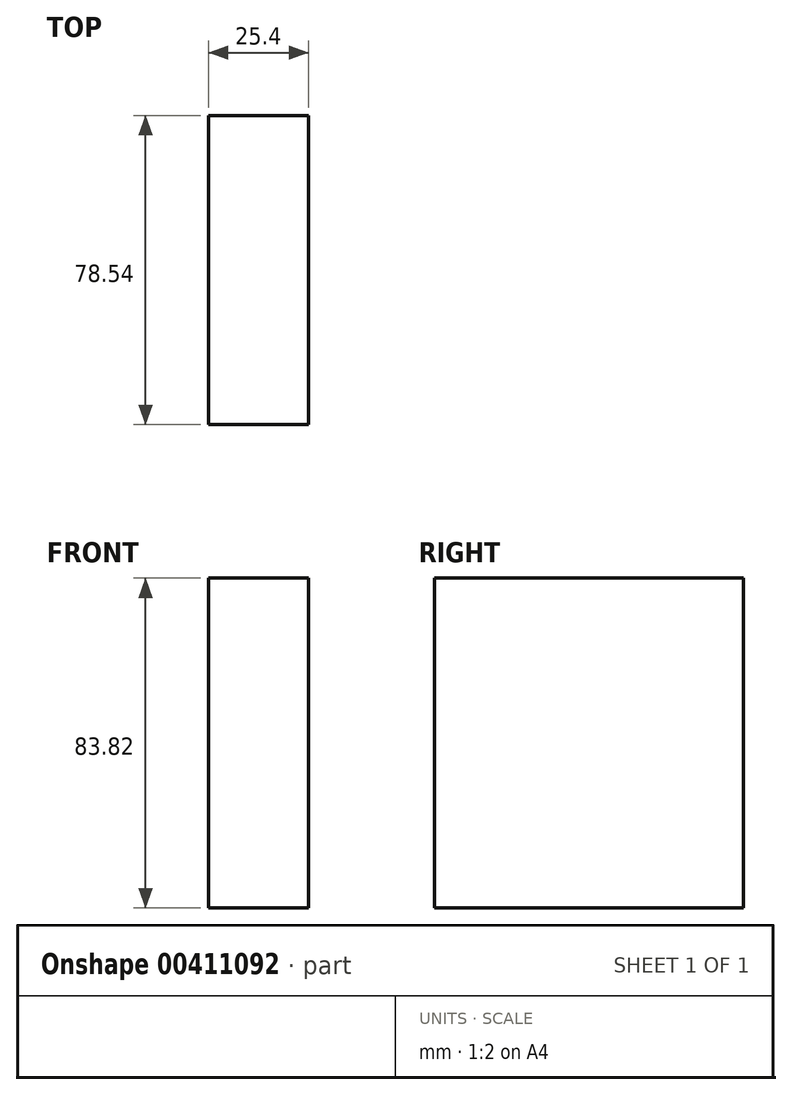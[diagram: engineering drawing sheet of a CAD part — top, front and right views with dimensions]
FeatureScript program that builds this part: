
annotation { "Feature Type Name" : "Feature", "Feature Type Description" : "" }
export const myFeature = defineFeature(function(context is Context, id is Id, definition is map)
    precondition{}
    {
        {
            var Q0;
            Q0=qCreatedBy(makeId("Right.planeOp"),FACE);
            var sketch = newSketch(context, id + "F0", { "sketchPlane" : qUnion([Q0])});
            skLineSegment(sketch, "E0.bottom", {"start": v(-45.09, -46.2) * mm, "end": v(45.09, -46.2) * mm});
            skLineSegment(sketch, "E0.top", {"start": v(-45.09, 46.2) * mm, "end": v(45.09, 46.2) * mm});
            skLineSegment(sketch, "E0.left", {"start": v(-45.09, -46.2) * mm, "end": v(-45.09, 46.2) * mm});
            skLineSegment(sketch, "E0.right", {"start": v(45.09, -46.2) * mm, "end": v(45.09, 46.2) * mm});
            skPoint(sketch, "E0.middle", {"position": v(0, 0) * mm});
            skSolve(sketch);
        }
        {
            var Q0;
            Q0 = qSketchRegion(id + "F0", true);
            extrude(context, id + "F1", {"entities" : qUnion([Q0]), "depth" : 25.4 * mm});
        }
        {
            var Q0;
            Q0=makeQuery(id+"F1.opExtrude","CAP_FACE",FACE,{"disambiguationData":[OSD([sQuery(id+"F0.wireOp",EDGE,"E0.bottom"),sQuery(id+"F0.wireOp",EDGE,"E0.top"),sQuery(id+"F0.wireOp",EDGE,"E0.left"),sQuery(id+"F0.wireOp",EDGE,"E0.right")])],"isStart":true});
            var sketch = newSketch(context, id + "F2", { "sketchPlane" : qUnion([Q0])});
            skLineSegment(sketch, "E1.bottom", {"start": v(39.27, -41.9) * mm, "end": v(-39.27, -41.9) * mm});
            skLineSegment(sketch, "E1.top", {"start": v(39.27, 41.9) * mm, "end": v(-39.27, 41.9) * mm});
            skLineSegment(sketch, "E1.left", {"start": v(39.27, -41.9) * mm, "end": v(39.27, 41.9) * mm});
            skLineSegment(sketch, "E1.right", {"start": v(-39.27, -41.9) * mm, "end": v(-39.27, 41.9) * mm});
            skPoint(sketch, "E1.middle", {"position": v(0, 0) * mm});
            skSolve(sketch);
        }
        {
            var Q0;
            Q0=makeQuery(id+"F2.imprint","IMPRINT",FACE,{"disambiguationData":[TD([[makeQuery(id+"F2.imprint","IMPRINT",EDGE,{"derivedFrom":sQuery(id+"F2.wireOp",EDGE,"E1.bottom")}),1.0]])]});
            extrude(context, id + "F3", {"entities" : qUnion([Q0]), "operationType" : NewBodyOperationType.REMOVE, "oppositeDirection" : true, "depth" : 63.5 * mm});
        }
    });
